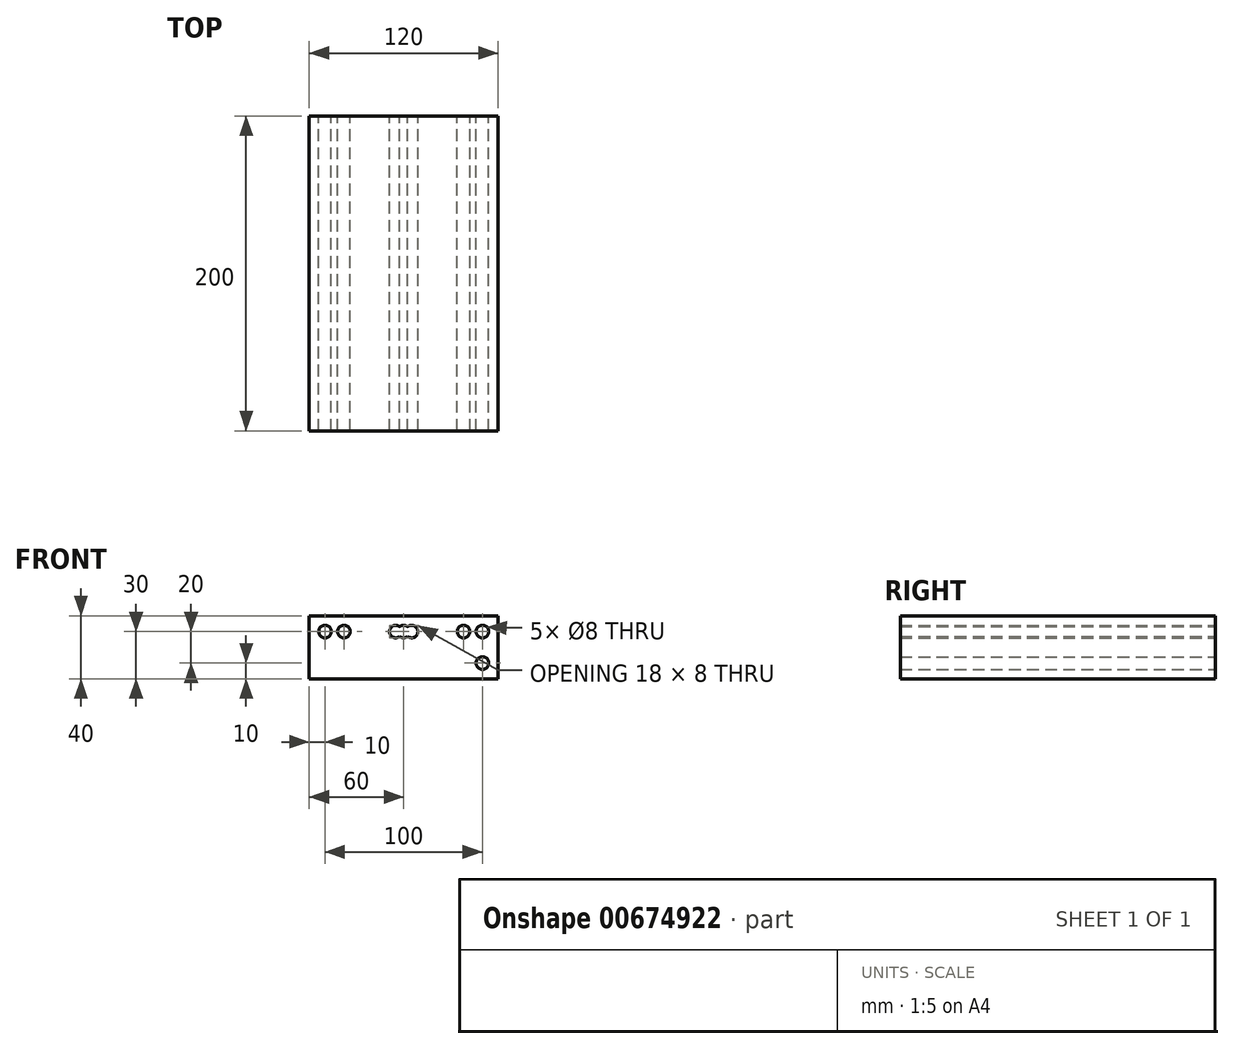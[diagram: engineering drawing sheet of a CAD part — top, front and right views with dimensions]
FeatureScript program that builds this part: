
annotation { "Feature Type Name" : "Feature", "Feature Type Description" : "" }
export const myFeature = defineFeature(function(context is Context, id is Id, definition is map)
    precondition{}
    {
        {
            var Q0;
            Q0=qCreatedBy(makeId("Front.planeOp"),FACE);
            var sketch = newSketch(context, id + "F0", { "sketchPlane" : qUnion([Q0])});
            skLineSegment(sketch, "E0.bottom", {"start": v(60, 20) * mm, "end": v(-60, 20) * mm});
            skLineSegment(sketch, "E0.top", {"start": v(60, -20) * mm, "end": v(-60, -20) * mm});
            skLineSegment(sketch, "E0.left", {"start": v(60, 20) * mm, "end": v(60, -20) * mm});
            skLineSegment(sketch, "E0.right", {"start": v(-60, 20) * mm, "end": v(-60, -20) * mm});
            skPoint(sketch, "E0.middle", {"position": v(0, 0) * mm});
            skCircle(sketch, "E1", {"center": v(-50, 10) * mm, "radius": 4 * mm});
            skCircle(sketch, "E2.MirrorC", {"center": v(50, 10) * mm, "radius": 4 * mm});
            skCircle(sketch, "E3", {"center": v(5, 10) * mm, "radius": 4 * mm});
            skCircle(sketch, "E4", {"center": v(0, 10) * mm, "radius": 4 * mm});
            skCircle(sketch, "E5", {"center": v(-38, 10) * mm, "radius": 4 * mm});
            skCircle(sketch, "E6.MirrorC", {"center": v(-5, 10) * mm, "radius": 4 * mm});
            skCircle(sketch, "E7.MirrorC", {"center": v(38, 10) * mm, "radius": 4 * mm});
            skCircle(sketch, "E8.MirrorC", {"center": v(50, -10) * mm, "radius": 4 * mm});
            skSolve(sketch);
        }
        {
            var Q0;
            Q0 = qSketchRegion(id + "F0", true);
            extrude(context, id + "F1", {"entities" : qUnion([Q0]), "depth" : 200 * mm, "offsetDistance" : 25 * mm});
        }
    });
